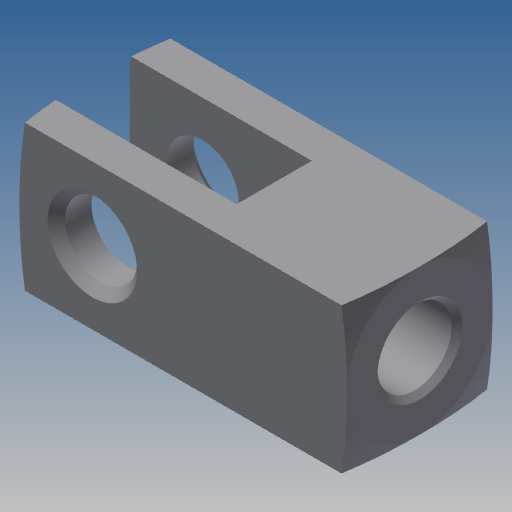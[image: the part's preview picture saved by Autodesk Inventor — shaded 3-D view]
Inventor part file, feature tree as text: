
AUTODESK INVENTOR PART (.ipt)
format: ipt  version: 2020 (Build 240168000, 168)  size: 226,816 bytes
history: native  units: in
note: dims shown in document units (in); Inventor stores cm internally (conversion verified against a paired STEP export)
features: other x126, sketch x7, revolve x4, extrude x2, hole x1
ambient origin geometry x8: Origin, YZ Plane, XZ Plane, XY Plane, X Axis, Y Axis, Z Axis, Center Point
bodies: Solid1 (feature_tree)
feature tree (140):
  extrude  "Extrusion1"  Depth=0.75in TaperAngle=0.0deg
  extrude  "Extrusion2"  TaperAngle=360.0deg  [1 undecoded]
  revolve  "Revolution1"  Angle=360.0deg
  hole  "Hole1"  [1 undecoded]
  revolve  "Revolution2"  [1 undecoded]
  revolve  "Revolution3"  [1 undecoded]
  revolve  "Revolution4"  [1 undecoded]
  other  "dummy_XY"
  other  "dummy_YZ"
  other  "dummy_ZX"
  other  "dummy_X"
  other  "dummy_Y"
  other  "dummy_Z"
  other  "dummy_Center"
  other  "h1_XY"
  other  "h1_YZ"
  other  "h1_ZX"
  other  "h1_X"
  other  "h1_Y"
  other  "h1_Z"
  other  "h1_Center"
  other  "h2_XY"
  other  "h2_YZ"
  other  "h2_ZX"
  other  "h2_X"
  other  "h2_Y"
  other  "h2_Z"
  other  "h2_Center"
  other  "l1_XY"
  other  "l1_YZ"
  other  "l1_ZX"
  other  "l1_X"
  other  "l1_Y"
  other  "l1_Z"
  other  "l1_Center"
  other  "l11_XY"
  other  "l11_YZ"
  other  "l11_ZX"
  other  "l11_X"
  other  "l11_Y"
  other  "l11_Z"
  other  "l11_Center"
  other  "l12_XY"
  other  "l12_YZ"
  other  "l12_ZX"
  other  "l12_X"
  other  "l12_Y"
  other  "l12_Z"
  other  "l12_Center"
  other  "l2_XY"
  other  "l2_YZ"
  other  "l2_ZX"
  other  "l2_X"
  other  "l2_Y"
  other  "l2_Z"
  other  "l2_Center"
  other  "l21_XY"
  other  "l21_YZ"
  other  "l21_ZX"
  other  "l21_X"
  other  "l21_Y"
  other  "l21_Z"
  other  "l21_Center"
  other  "l22_XY"
  other  "l22_YZ"
  other  "l22_ZX"
  other  "l22_X"
  other  "l22_Y"
  other  "l22_Z"
  other  "l22_Center"
  other  "piston_rod_clevis_XY"
  other  "piston_rod_clevis_YZ"
  other  "piston_rod_clevis_ZX"
  other  "piston_rod_clevis_X"
  other  "piston_rod_clevis_Y"
  other  "piston_rod_clevis_Z"
  other  "piston_rod_clevis_Center"
  other  "rod_clevis_body_XY"
  other  "rod_clevis_body_YZ"
  other  "rod_clevis_body_ZX"
  other  "rod_clevis_body_X"
  other  "rod_clevis_body_Y"
  other  "rod_clevis_body_Z"
  other  "rod_clevis_body_Center"
  other  "th1_XY"
  other  "th1_YZ"
  other  "th1_ZX"
  other  "th1_X"
  other  "th1_Y"
  other  "th1_Z"
  other  "th1_Center"
  other  "th2_XY"
  other  "th2_YZ"
  other  "th2_ZX"
  other  "th2_X"
  other  "th2_Y"
  other  "th2_Z"
  other  "th2_Center"
  other  "to_cylinder_XY"
  other  "to_cylinder_YZ"
  other  "to_cylinder_ZX"
  other  "to_cylinder_X"
  other  "to_cylinder_Y"
  other  "to_cylinder_Z"
  other  "to_cylinder_Center"
  other  "w1_XY"
  other  "w1_YZ"
  other  "w1_ZX"
  other  "w1_X"
  other  "w1_Y"
  other  "w1_Z"
  other  "w1_Center"
  other  "w11_XY"
  other  "w11_YZ"
  other  "w11_ZX"
  other  "w11_X"
  other  "w11_Y"
  other  "w11_Z"
  other  "w11_Center"
  other  "w12_XY"
  other  "w12_YZ"
  other  "w12_ZX"
  other  "w12_X"
  other  "w12_Y"
  other  "w12_Z"
  other  "w12_Center"
  other  "w2_XY"
  other  "w2_YZ"
  other  "w2_ZX"
  other  "w2_X"
  other  "w2_Y"
  other  "w2_Z"
  other  "w2_Center"
  sketch  "Sketch_1"  dims[d0=0.75in d1=0.0in d2=0.75in d3=0.0in]
  sketch  "Sketch_2"  dims[d4=360.0deg]
  sketch  "Sketch_3"  dims[d5=0.3906in d6=0.75in d7=0.375in d8=0.25in d9=0.5635in d10=0.13in d11=0.0in d12=360.0deg]
  sketch  "Sketch5"  dims[d13=360.0deg d14=360.0deg]
  sketch  "Sketch_5"  dims[d15=0.0in d16=0.0in]
  sketch  "Sketch_9"
  sketch  "Sketch_10"
note: 5 required parameter values undecoded (feature->parameter linkage not recoverable at this tier; creation-order binding heuristic only, values carry confidence <= 0.55)
